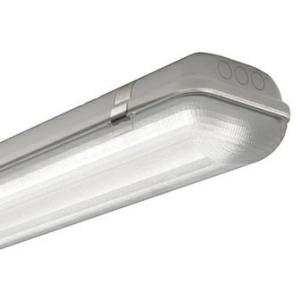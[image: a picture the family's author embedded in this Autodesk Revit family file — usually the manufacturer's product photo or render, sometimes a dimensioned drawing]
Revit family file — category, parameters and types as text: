
# Revit family: 3f_filippi_-_3f_linda_3f_filippi_-_58623_-_3f_linda_led_2x30w_ep_l1570
name_source: partatom
category: Lighting Fixtures
units: mm (PartAtom-declared; Revit-internal decimal feet)

## family parameters
Cut with Voids When Loaded = No
Host = Face
Light Source = No
Part Type = Normal
Room Calculation Point = No
Round Connector Dimension = Use Diameter
Shared = No

## types (1)
- 3F Filippi - 3F Linda (1 x LED, 9715 lm, 67 W, 4000 K)
    Apparent Load = 67 VA
    Approval mark = ENEC
    CIE Flux Codes = 46 76 93 97 100
    Color Rendering = 80
    Color Temperature = 4000 K
    Control Gear = Electronic ballast
    Default Elevation = 1800 mm
    Description = ILLUMINOTECHNICAL
Luminous efficiency 100% (DLOR 97%, ULOR 3%).
Initial luminous flux of the luminaire 9715 lm.
Emergency luminaire luminous flux BLF 5.7%.
Controlled symmetric distribution.
Installation Interdistance Transv.D = 1.52 x hu - Long.D = 1.17 x hu.
Tabular UGR (CIE 117 - 4H-8H; S=0.25H; 70/50/20): RUG 24.3 - 23.5.
Beam angle: 94° - 78°.
Luminous efficacy 145 lm/W.
Lifetime (L93/B10): 30000 h. (tq+25°C)
Lifetime (L90/B10): 50000 h. (tq+25°C)
Lifetime (L85/B10): 80000 h. (tq+25°C)
Lifetime (L80/B10): 100000 h. (tq+25°C)
Sudden decreased luminous flux after 50000 hours: 0% (C0).
Photobiological safety in compliance with IEC/TR 62778: RG0 risk exempt, (IEC 62471).
In compliance with IEC/EN 62722-2-1 - IEC/EN 62717 standards.

SOURCE
2 linear LED modules 30W/840.
Energy efficiency class (UE 2019/2020 - UE 2019/2015): D.
CIE 13.3 Colour rendering index: CRI >80 (R9 <50%).
IES TM-30 Fidelity Index: Rf = 84 Rg = 95.
CCT nominal colour temperature 4000 K.
Colour initial tolerance (MacAdam): SDCM 3.

MECHANICAL
Self-extinguishing V2 polycarbonate housing, injection moulded, RAL 7035 grey.
Ecologic anti-aging injected sealing gasket.
Diffuser in self-extinguishing V2 polycarbonate, photo-engraved interior, UV stabilised, injection moulded with smooth outer surface, tamper-proof opening.
Gear-holder reflector in hot-dip galvanised steel, painted with white polyester base.
Snug fit safety snap-lock clips for diffuser mounting in stainless steel, screwdriver opening.
Fixing brackets in stainless steel.
Possibility for technicians to access the interior of the luminaire.
Luminaire with limited surface temperature. - D - (EN 60598-2-24)
Dimensions: 1570x160 mm, height 100 mm. Weight 3.903 kg.
IP66 protection degree.
Mechanical strength to impacts IK10 (20 joule).
Glow-wire test resistance 850°C.

ELECTRICAL
Halogen Free electronic wiring 230V-50/60Hz, power factor 0.90, THD <25%, constant output current, SELV, class I, 1 driver.
Power of the luminaire 67 W.
CE - IEC 60598-1 - EN 60598-1.
EP maintained emergency wiring on board, 1h duration, 24h recharge; compliant with EN 60598-2-22, excluding high risk areas.
SAFE FLICKER: PstLM=<1 and SVM=<0.4 (IEC TR 61547-1 and IEC TR 63158), to ensure a more comfortable and safe light.
Ambient temperature from +5°C to +25°C.
Temperature class T6 max 85°C.
Relative humidity UR: <85%.

INSTALLATION
Ceiling / Suspended / Wall.
All accessories dedicated to this product are available on the Catalog and on our website www.3F-Filippi.com.

APPLICATIONS
Suitable product for food production plants (HACCP), IFS (Food Version 6), BRC (GSFS Food Version 7).
Dry, dusty indoor environments, subject to occasional water splashes.
Virtually shatterproof polycarbonate compatibly with the fumes / atmospheres that compromise the elasticity of plastic materials.
Not suitable for installation on surfaces subject to important vibrations, exposed to weather conditions, on ropes or poles.
Suitable for illumination of public car parks and parking grounds referred to DIN 67528:2018-04.

WARNING
Fixture not suitable for cold stores with an ambient temperature <5°C and/or relative humidity >85%.
Luminaire designed for disposal/recycling at end-of-life.
Replaceable (LED only) light source by a professional. Replaceable control gear by a professional.
    Height = 100 mm  [stored 0.328084 ft]
    Lamp = 1 x LED
    Lamp Light Flux = 9715 lm
    Lamp Power = 67 W
    Lamp count = 1
    Length = 1570 mm
    Lifetime = 50000 h
    Luminous efficacy = 145 lm/W
    Manufacturer = 3F Filippi
    ModVariant = No
    Model = 3F Filippi - 58623 - 3F Linda LED 2x30W EP L1570
    Mounting Place = Ceiling
    Mounting Type = Pendant
    Number of Poles = 1
    OnlyDefault = Yes
    Power Factor = 1
    Product Name = 3F Filippi - 3F Linda
    Product group = pendant luminaire
    ProductGroupID = 9
    Protection Class = Protection class I
    Protection Degree = IP 66
    RLX_Detail_Level = 1
    RLX_Emergency_Light_Flux = 0 lm
    RLX_Emergency_Type = 0
    RLX_Emergency_Type_DB = No
    RlxData = <blob elided: 71325 chars, md5=48c6e09d>
    Socket = socket
    Standby Power = 0 W
    System Light Flux = 9715 lm
    System Power = 67 W
    Type Comments = Product without accessories
    Type Image = 3ffilippi_3f_linda_led_2x.jpg
    URL = http://relux.com
    VarID = ---
    Voltage = 0 V
    Weight = 0.00 kg
    Width = 160 mm

note: [stored X ft] marks values corroborated as IEEE doubles in the binary element streams (Revit-internal decimal feet)

## geometry (parser evidence)
native form markers: Blend x4, Sweep x9
no freeform markers — native parametric forms only
